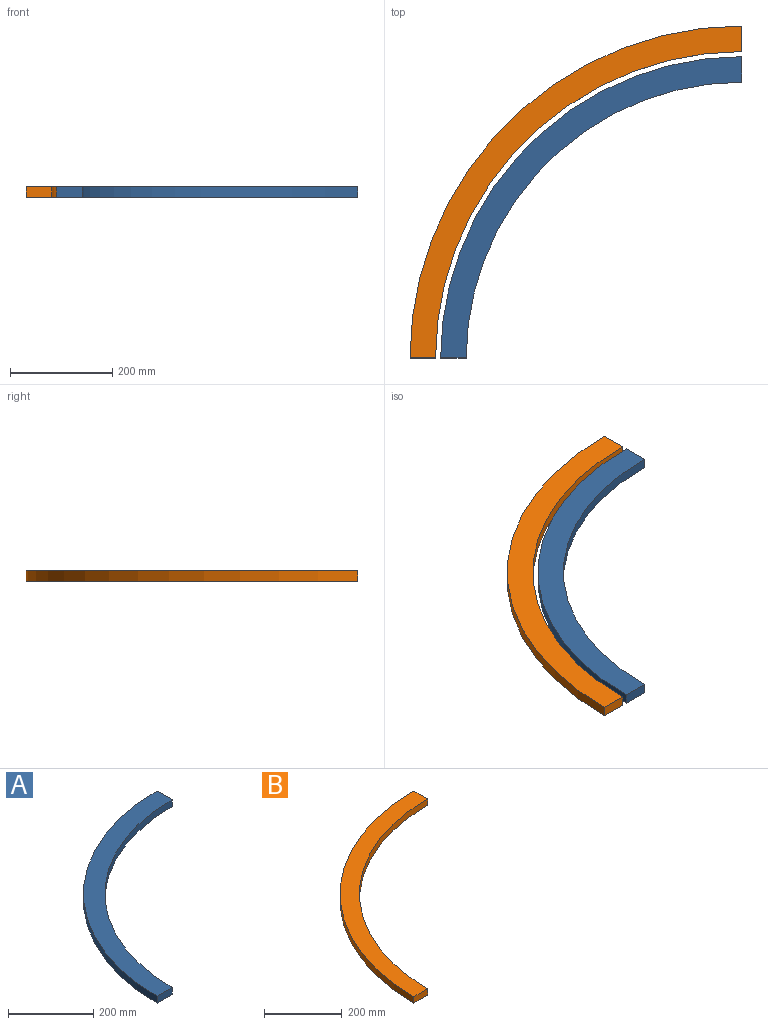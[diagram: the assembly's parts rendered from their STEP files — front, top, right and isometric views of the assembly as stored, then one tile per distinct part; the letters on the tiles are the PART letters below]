
ASSEMBLY  parts=2 mates=1
PART A: 6 faces, bbox 590x590x20 mm
  f0: plane 50x20mm, normal (1,0,0), area 1000mm2, adj f1,f3,f4,f5
  f1: cylinder r=590mm len=590mm, axis (0,0,-1), area 18535.4mm2, adj f0,f2,f4,f5
  f2: plane 50x20mm, normal (0,-1,0), area 1000mm2, adj f1,f3,f4,f5
  f3: cylinder r=540mm len=540mm, axis (0,0,-1), area 16964.6mm2, adj f0,f2,f4,f5
  f4: plane 590x590mm, normal (0,0,1), area 44375mm2, adj f0,f1,f2,f3
  f5: plane 590x590mm, normal (0,0,-1), area 44375mm2, adj f0,f1,f2,f3
PART B: 6 faces, bbox 650x650x20 mm
  f0: plane 50x20mm, normal (1,0,0), area 1000mm2, adj f1,f3,f4,f5
  f1: cylinder r=650mm len=650mm, axis (0,0,-1), area 20420.4mm2, adj f0,f2,f4,f5
  f2: plane 50x20mm, normal (0,-1,0), area 1000mm2, adj f1,f3,f4,f5
  f3: cylinder r=600mm len=600mm, axis (0,0,-1), area 18849.6mm2, adj f0,f2,f4,f5
  f4: plane 650x650mm, normal (0,0,1), area 49087.4mm2, adj f0,f1,f2,f3
  f5: plane 650x650mm, normal (0,0,-1), area 49087.4mm2, adj f0,f1,f2,f3
PLACE A at identity
PLACE B at identity
MATE fastened B.f1 <-> A.f1  axis (0,0,1) through (0,0,20)mm
